# Revit family: Electronics_Masking-Loudspeakers_Biamp_Cambridge_Active-Emitter-Sound-Masking-Loudspeaker_QT__
name_source: partatom
category: Communication Devices
units: mm (PartAtom-declared; Revit-internal decimal feet)

## family parameters
Cut with Voids When Loaded = Yes
Host = Face
Maintain Annotation Orientation = No
OmniClass Number = 23.85.10.11.11.21
OmniClass Title = Speakers
Part Type = Normal
Room Calculation Point = No
Round Connector Dimension = Use Diameter
Shared = No

## types (4) — shared parameters
Channel Selection = 4 Auto-Sequencing and Repeating Channels
Default Elevation = 48 "
Diameter = 3.25 "
Driver Diameter = 1 1/4''
I/O Connectors = 2 RJ-45 connectors
Manufacturer = Biamp
Minimum Masking SPL = 30dBA
Nominal Dispersion = 170° conical / half space
Product Documentation Link = https://downloads.biamp.com
Product Page URL = https://www.biamp.com
Product data url = https://www.bimobject.com
URL = https://www.biamp.com
Weight = 0.40 lbf

## per-type parameters (varying)
| type | Active | Active (Black Grid) | Active (White Grid) | Compliance | Depth | Description | Enclosure | Housing Material | Included Accessories | Loudspeaker Type | Maximum Masking SPL | Maximum Music/Paging SPL | Model | Music/Paging Frequency Response | Nominal Impedance | Qt Emitter | Selectable Attenuation | Sound Masking Frequency Response |
| Qt Emitter White | No | No | No | ETL listed (USA and Canada), CE Marked (Europe), RoHS Directive (Europe), Evaluated to the requirements of UL 1480a and UL 2043 and is suitable for use in air handling spaces | 2.5 " | QT® Emitter Sound Masking Loudspeaker | Sealed | Biamp - Plastic - White | Acoustic Ceiling Tile Mounting Ring, UTP Cable (16ft/30ft) | Passive with transformer | 57dBA | 56dBA | Qt Emitter | 200Hz to 10kHz | 3.6 kohm | Yes | 0 dB, -3 dB, -6 dB, -9 dB | 200Hz to 6.3kHz |
| Qt Active Emitter White | Yes | No | Yes | ETL listed (USA and Canada), Evaluated to the requirements of UL 2043 and is suitable for use in air handling spaces | 3.5 " | QT® Active Emitter Sound Masking Loudspeaker | Front Vented | Biamp - Plastic - White | Acoustic Ceiling Tile Mounting Ring, UTP Cable (16ft/25ft/30ft) | Active with integrated amplifier | 60dBA | 74dBA | Qt Active Emitter | 115Hz to 12kHz | 40 kohm | No | 0 dB, -1.5 dB, -3 dB, -4.5 dB | 125Hz to 10kHz |
| Qt Active Emitter Black | Yes | Yes | No | ETL listed (USA and Canada), Evaluated to the requirements of UL 2043 and is suitable for use in air handling spaces | 3.5 " | QT® Active Emitter Sound Masking Loudspeaker | Front Vented | Biamp - Plastic - Black | Acoustic Ceiling Tile Mounting Ring, UTP Cable (16ft/25ft/30ft) | Active with integrated amplifier | 60dBA | 74dBA | Qt Active Emitter | 115Hz to 12kHz | 40 kohm | No | 0 dB, -1.5 dB, -3 dB, -4.5 dB | 125Hz to 10kHz |
| Qt Emitter Black | No | No | No | ETL listed (USA and Canada), CE Marked (Europe), RoHS Directive (Europe), Evaluated to the requirements of UL 1480a and UL 2043 and is suitable for use in air handling spaces | 2.5 " | QT® Emitter Sound Masking Loudspeaker | Sealed | Biamp - Plastic - Black | Acoustic Ceiling Tile Mounting Ring, UTP Cable (16ft/30ft) | Passive with transformer | 57dBA | 56dBA | Qt Emitter | 200Hz to 10kHz | 3.6 kohm | Yes | 0 dB, -3 dB, -6 dB, -9 dB | 200Hz to 6.3kHz |

## geometry (parser evidence)
native form markers: Sweep x2
no freeform markers — native parametric forms only
